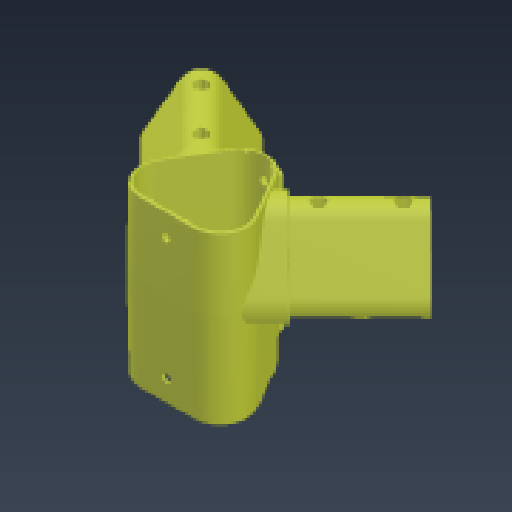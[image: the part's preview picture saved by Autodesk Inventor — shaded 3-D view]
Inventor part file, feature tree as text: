
AUTODESK INVENTOR PART (.ipt)
format: ipt  version: 2024.3 (Build 283343000, 343)  size: 2,895,872 bytes
history: native  units: in
note: dims shown in document units (in); Inventor stores cm internally (conversion verified against a paired STEP export)
features: mirror x1
ambient origin geometry x8: Origin, YZ Plane, XZ Plane, XY Plane, X Axis, Y Axis, Z Axis, Center Point
bodies: Solid1 (feature_tree)
feature tree (1):
  mirror  "Mirror2"
